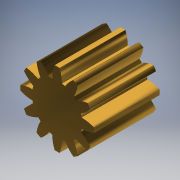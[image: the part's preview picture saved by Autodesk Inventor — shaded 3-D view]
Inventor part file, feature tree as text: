
AUTODESK INVENTOR PART (.ipt)
format: ipt  version: 2019 (Build 230136000, 136)  size: 201,216 bytes
history: native  units: mm (DEFAULTED — no unit token found)
features: plane x3, other x3, sketch x2, extrude x1
ambient origin geometry x8: Origin, YZ Plane, XZ Plane, XY Plane, X Axis, Y Axis, Z Axis, Center Point
bodies: Solid1 (feature_tree)
feature tree (9):
  extrude  "Extrusion1"  Depth=2.5mm TaperAngle=0.0deg
  plane  "Work Plane2"
  plane  "Work Plane8"
  plane  "Work Plane9"
  other  "Spur Gear"
  sketch  "Sketch1"  dims[d0=2.799202mm d1=2.5mm d2=0.0mm]
  sketch  "Sketch2"  dims[d3=2.39mm d4=10.0mm d5=0.0mm d16=5.975mm d17=0.0mm d34=15.0deg d39=0.0mm d41=0.0mm d43=5.975mm d46=5.975mm d47=0.0mm d48=0.0mm]
  other  "Srf1"
  other  "Pitch Diameter"
